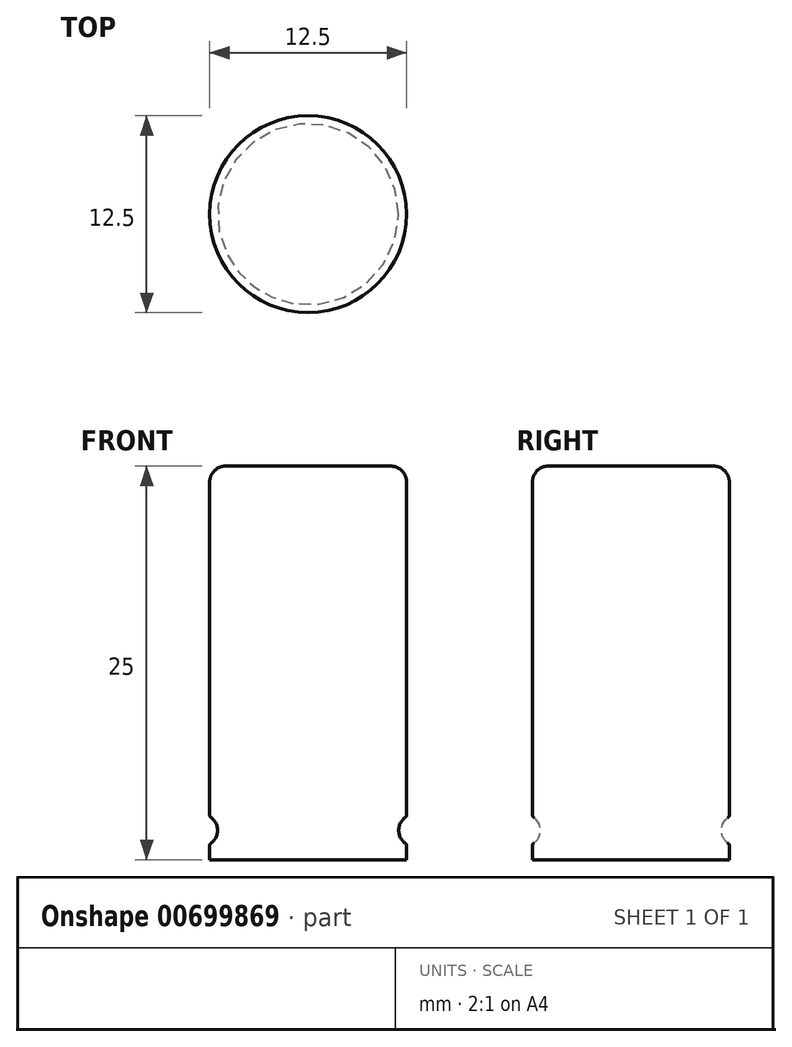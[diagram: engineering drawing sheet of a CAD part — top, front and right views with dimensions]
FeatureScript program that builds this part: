
annotation { "Feature Type Name" : "Feature", "Feature Type Description" : "" }
export const myFeature = defineFeature(function(context is Context, id is Id, definition is map)
    precondition{}
    {
        {
            var Q0;
            Q0=qCreatedBy(makeId("Front.planeOp"),FACE);
            var sketch = newSketch(context, id + "F0", { "sketchPlane" : qUnion([Q0])});
            skLineSegment(sketch, "E0", {"start": v(0, 0) * mm, "end": v(6.25, 0) * mm});
            skLineSegment(sketch, "E1", {"start": v(6.25, 0) * mm, "end": v(6.25, 0.9) * mm});
            skLineSegment(sketch, "E2", {"start": v(6.25, 2.84) * mm, "end": v(6.25, 24) * mm});
            skLineSegment(sketch, "E3", {"start": v(5.25, 25) * mm, "end": v(0, 25) * mm});
            skPoint(sketch, "E4.visualSharp", {"position": v(6.25, 25) * mm});
            skArc(sketch, "E4.filletArc", {"start": v(6.25, 24) * mm, "mid": v(5.96, 24.7) * mm, "end": v(5.25, 25) * mm});
            skArc(sketch, "E5", {"start": v(6.17, 1.05) * mm, "mid": v(5.75, 1.87) * mm, "end": v(6.17, 2.68) * mm});
            skLineSegment(sketch, "E6", {"start": v(0, 25) * mm, "end": v(0, 0) * mm});
            skPoint(sketch, "E7.visualSharp", {"position": v(6.25, 2.73) * mm});
            skArc(sketch, "E7.filletArc", {"start": v(6.17, 2.68) * mm, "mid": v(6.23, 2.75) * mm, "end": v(6.25, 2.84) * mm});
            skPoint(sketch, "E8.visualSharp", {"position": v(6.25, 1) * mm});
            skArc(sketch, "E8.filletArc", {"start": v(6.25, 0.9) * mm, "mid": v(6.23, 0.98) * mm, "end": v(6.17, 1.05) * mm});
            skSolve(sketch);
        }
        {
            var Q0;
            Q0=makeQuery(id+"F0.imprint","IMPRINT",FACE,{"disambiguationData":[TD([[makeQuery(id+"F0.imprint","IMPRINT",EDGE,{"derivedFrom":sQuery(id+"F0.wireOp",EDGE,"E0")}),1.0]])]});
            var Q1;
            Q1=sQuery(id+"F0.wireOp",EDGE,"E6");
            revolve(context, id + "F1", {"entities" : qUnion([Q0]), "axis" : qUnion([Q1]), "revolveType" : RevolveType.FULL});
        }
    });
